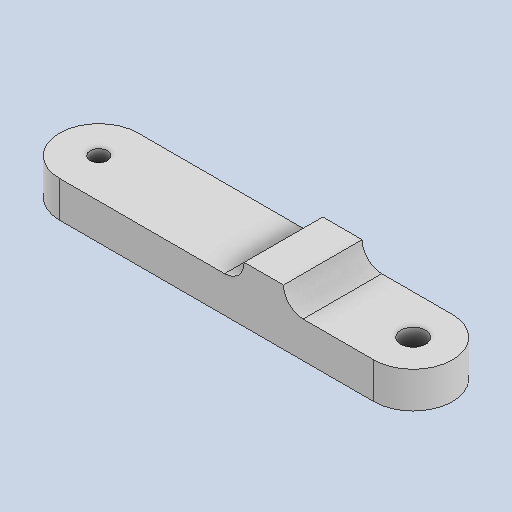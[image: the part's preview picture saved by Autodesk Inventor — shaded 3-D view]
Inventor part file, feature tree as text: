
AUTODESK INVENTOR PART (.ipt)
format: ipt  version: 2022 (Build 260153000, 153)  size: 102,400 bytes
history: native  units: in
note: dims shown in document units (in); Inventor stores cm internally (conversion verified against a paired STEP export)
features: fillet x1
ambient origin geometry x8: Origin, YZ Plane, XZ Plane, XY Plane, X Axis, Y Axis, Z Axis, Center Point
bodies: Solid1 (feature_tree)
feature tree (1):
  fillet  "Fillet1"  [1 undecoded]
note: 1 required parameter value undecoded (feature->parameter linkage not recoverable at this tier; creation-order binding heuristic only, values carry confidence <= 0.55)
